# Revit family: ADLQ-235-xxx-8xx-SMx
name_source: partatom
category: Oprawy oświetleniowe
revit_build: Autodesk Revit 2017 (Build: 20190508_0315(x64)
units: mm (PartAtom-declared; Revit-internal decimal feet)

## family parameters
Numer OmniClass = 23.80.70.11
Obiekt nadrzędny = Powierzchnia
Punkt obliczania pomieszczeń = Nie
Tnij formami wycięć po wczytaniu = Nie
Typ części = Normalny
Tytuł OmniClass = Luminaries for Internal Lighting
Współdzielony = Nie
Wymiar okrągłego złącza = Użyj średnicy
Źródło światła = Tak

## types (8) — shared parameters
Emituj kształt widoczny w renderingu = Nie
Emituj z długości prostokąta = 210 mm  [stored 0.688976 ft]
Emituj z szerokości prostokąta = 210 mm  [stored 0.688976 ft]
Filtr koloru = 16777215
Kod zespołu = D5020200
Lampa = LED
Odchylenie kierunku = 90.00°
Producent = RIDI Leuchten GmbH
URL = www.ridi.de
Zmiana temperatury barwowej przyciemniania lampy = <Brak>
brand = RIDI
conformity mark = CE
electrical safety class = 1
height = 228 mm  [stored 0.748031 ft]
ingress protection (IP) code = IP20
length = 235 mm  [stored 0.770997 ft]
nominal frequency = 50-60Hz
nominal voltage = 230
voltage type (AC, DC, UC) = AC
weight = 2.93 kg
width = 235 mm  [stored 0.770997 ft]
zero-valued in all types: Domyślna rzędna

## per-type parameters (varying)
| type | Model | Obciążenie pozorne | Plik sieci fotometrycznej | rated input power |
| ADLQ 235/2000-830 SM | 0321935 | 16 VA | ADLQ 2352000-840 SM.IES | 16 |
| ADLQ 235/2000-830 SM-DALI | 0331935 | 16 VA | ADLQ 2352000-840 SM.IES | 16 |
| ADLQ 235/2000-840 SM | 0321936 | 16 VA | ADLQ 2352000-840 SM.IES | 16 |
| ADLQ 235/2000-840 SM-DALI | 0331936 | 16 VA | ADLQ 2352000-840 SM.IES | 16 |
| ADLQ 235/3000-830 SM | 0321937 | 23 VA | ADLQ 2353000-840 SM.IES | 23 |
| ADLQ 235/3000-830 SM-DALI | 0331937 | 23 VA | ADLQ 2353000-840 SM.IES | 23 |
| ADLQ 235/3000-840 SM | 0321938 | 23 VA | ADLQ 2353000-840 SM.IES | 23 |
| ADLQ 235/3000-840 SM-DALI | 0331938 | 23 VA | ADLQ 2353000-840 SM.IES | 23 |

note: column(s) folded — value = type name in every type: product name

note: [stored X ft] marks values corroborated as IEEE doubles in the binary element streams (Revit-internal decimal feet)
